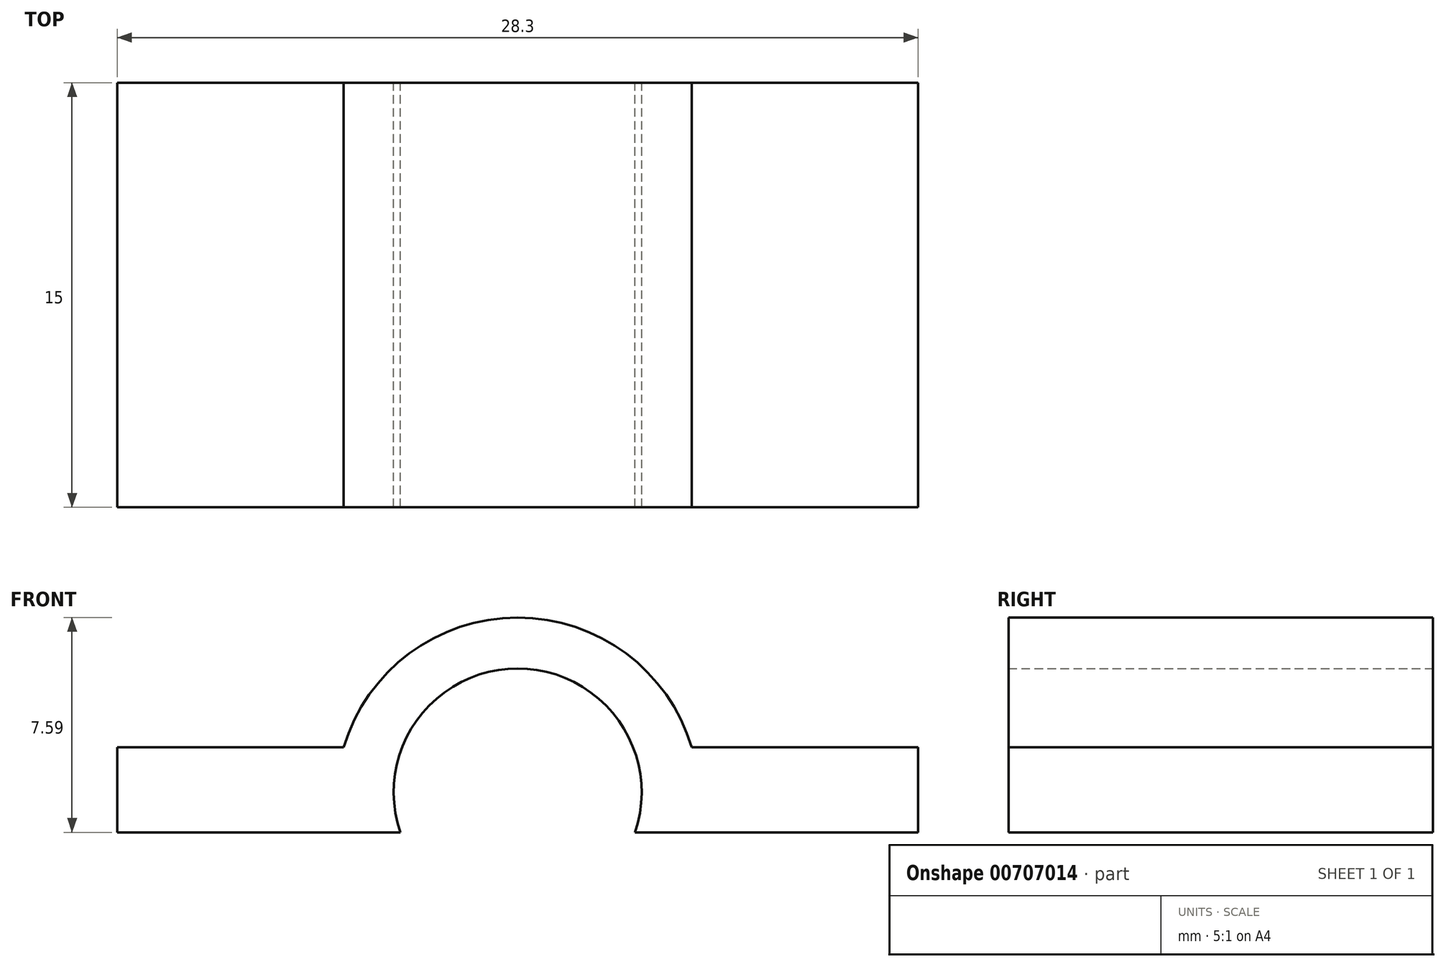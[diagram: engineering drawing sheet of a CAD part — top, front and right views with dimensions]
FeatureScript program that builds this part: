
annotation { "Feature Type Name" : "Feature", "Feature Type Description" : "" }
export const myFeature = defineFeature(function(context is Context, id is Id, definition is map)
    precondition{}
    {
        {
            var Q0;
            Q0=qCreatedBy(makeId("Front.planeOp"),FACE);
            var sketch = newSketch(context, id + "F0", { "sketchPlane" : qUnion([Q0])});
            skLineSegment(sketch, "E0", {"start": v(-14.15, 0) * mm, "end": v(-4.15, 0) * mm});
            skLineSegment(sketch, "E1", {"start": v(-14.15, 0) * mm, "end": v(-14.15, 3) * mm});
            skLineSegment(sketch, "E2", {"start": v(-14.15, 3) * mm, "end": v(-6.15, 3) * mm});
            skLineSegment(sketch, "E3", {"start": v(6.15, 3) * mm, "end": v(14.15, 3) * mm});
            skLineSegment(sketch, "E4", {"start": v(14.15, 3) * mm, "end": v(14.15, 0) * mm});
            skLineSegment(sketch, "E5", {"start": v(14.15, 0) * mm, "end": v(4.15, 0) * mm});
            skArc(sketch, "E6", {"start": v(6.15, 3) * mm, "mid": v(0, 7.59) * mm, "end": v(-6.15, 3) * mm});
            skArc(sketch, "E7", {"start": v(4.15, 0) * mm, "mid": v(0, 5.79) * mm, "end": v(-4.15, 0) * mm});
            skLineSegment(sketch, "E8", {"start": v(0, 1.4) * mm, "end": v(0, 0) * mm, "construction": true});
            skSolve(sketch);
        }
        {
            var Q0;
            Q0=makeQuery(id+"F0.imprint","IMPRINT",FACE,{"disambiguationData":[TD([[makeQuery(id+"F0.imprint","IMPRINT",EDGE,{"derivedFrom":sQuery(id+"F0.wireOp",EDGE,"E0")}),1.0]])]});
            extrude(context, id + "F1", {"entities" : qUnion([Q0]), "depth" : 15 * mm, "offsetDistance" : 25 * mm});
        }
    });
